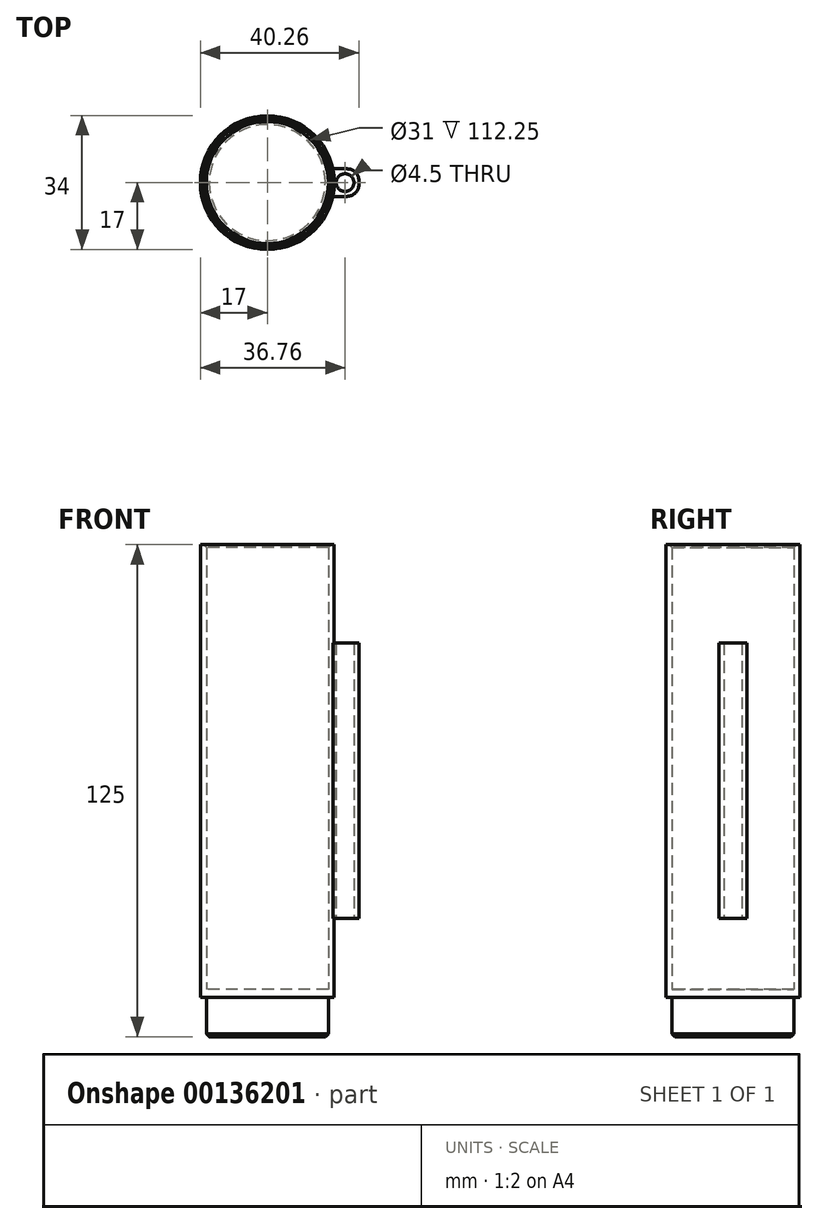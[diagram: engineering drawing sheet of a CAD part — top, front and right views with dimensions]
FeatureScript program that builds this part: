
annotation { "Feature Type Name" : "Feature", "Feature Type Description" : "" }
export const myFeature = defineFeature(function(context is Context, id is Id, definition is map)
    precondition{}
    {
        {
            var Q0;
            Q0=qCreatedBy(makeId("Top.planeOp"),FACE);
            cPlane(context, id + "F0", {"entities" : qUnion([Q0]), "cplaneType" : CPlaneType.OFFSET, "offset" : (107) * mm, "width" : 150 * mm, "height" : 150 * mm});
        }
        {
            var Q0;
            Q0=qCreatedBy(id+"F0.planeOp",FACE);
            var sketch = newSketch(context, id + "F1", { "sketchPlane" : qUnion([Q0])});
            skCircle(sketch, "E0", {"center": v(0, 0) * mm, "radius": 17 * mm});
            skCircle(sketch, "E1", {"center": v(0, 0) * mm, "radius": 15.5 * mm});
            skSolve(sketch);
        }
        {
            var Q0;
            Q0=qSketchRegion(id+"F1",true);
            extrude(context, id + "F2", {"entities" : qUnion([Q0]), "depth" : 115 * mm});
        }
        {
            var Q0;
            Q0=makeQuery(id+"F2.opExtrude","CAP_EDGE",EDGE,{"disambiguationData":[OSD([sQuery(id+"F1.wireOp",EDGE,"E1")])],"isStart":false});
            chamfer(context, id + "F3", {"entities" : qUnion([Q0]), "width" : .75 * mm, "tangentPropagation" : true});
        }
        {
            var Q0;
            Q0=qCreatedBy(id+"F0.planeOp",FACE);
            var sketch = newSketch(context, id + "F4", { "sketchPlane" : qUnion([Q0])});
            skCircle(sketch, "E2.0", {"center": v(0, 0) * mm, "radius": 17 * mm});
            skSolve(sketch);
        }
        {
            var Q0;
            Q0=makeQuery(id+"F4.imprint","IMPRINT",FACE,{"disambiguationData":[TD([[makeQuery(id+"F4.imprint","IMPRINT",EDGE,{"derivedFrom":sQuery(id+"F4.wireOp",EDGE,"E2.0")}),1.0]])]});
            extrude(context, id + "F5", {"entities" : qUnion([Q0]), "operationType" : NewBodyOperationType.ADD, "depth" : 2 * mm});
        }
        {
            var Q0;
            Q0=makeQuery(id+"F5.boolean.opBoolean","MERGE",FACE,{"derivedFrom":[makeQuery(id+"F2.opExtrude","CAP_FACE",FACE,{"disambiguationData":[OSD([sQuery(id+"F1.wireOp",EDGE,"E0"),sQuery(id+"F1.wireOp",EDGE,"E1")])],"isStart":true}),makeQuery(id+"F5.opExtrude","CAP_FACE",FACE,{"disambiguationData":[OSD([sQuery(id+"F4.wireOp",EDGE,"E2.0")])],"isStart":true})]});
            var sketch = newSketch(context, id + "F6", { "sketchPlane" : qUnion([Q0])});
            skCircle(sketch, "E3", {"center": v(0, 0) * mm, "radius": 15.5 * mm});
            skSolve(sketch);
        }
        {
            var Q0;
            Q0=qSketchRegion(id+"F6",true);
            extrude(context, id + "F7", {"entities" : qUnion([Q0]), "operationType" : NewBodyOperationType.ADD, "depth" : 10 * mm});
        }
        {
            var Q0;
            Q0=makeQuery(id+"F7.opExtrude","CAP_EDGE",EDGE,{"disambiguationData":[OSD([sQuery(id+"F6.wireOp",EDGE,"E3")])],"isStart":false});
            chamfer(context, id + "F8", {"entities" : qUnion([Q0]), "width" : .75 * mm, "tangentPropagation" : true});
        }
        {
            var Q0;
            Q0=qCreatedBy(id+"F0.planeOp",FACE);
            cPlane(context, id + "F9", {"entities" : qUnion([Q0]), "cplaneType" : CPlaneType.OFFSET, "offset" : 20 * mm, "width" : 150 * mm, "height" : 150 * mm});
        }
        {
            var Q0;
            Q0=qCreatedBy(id+"F9.planeOp",FACE);
            var sketch = newSketch(context, id + "F10", { "sketchPlane" : qUnion([Q0])});
            skLineSegment(sketch, "E4.bottom", {"start": v(16.26, 3.5) * mm, "end": v(20.26, 3.5) * mm});
            skLineSegment(sketch, "E4.top", {"start": v(16.26, -3.5) * mm, "end": v(20.26, -3.5) * mm});
            skLineSegment(sketch, "E4.left", {"start": v(16.26, 3.5) * mm, "end": v(16.26, -3.5) * mm});
            skLineSegment(sketch, "E4.right", {"start": v(23.26, 0.5) * mm, "end": v(23.26, -0.5) * mm});
            skPoint(sketch, "E5", {"position": v(16.26, 0) * mm});
            skCircle(sketch, "E6", {"center": v(19.76, 0) * mm, "radius": 2.25 * mm});
            skPoint(sketch, "E7.visualSharp", {"position": v(23.26, 3.5) * mm});
            skArc(sketch, "E7.filletArc", {"start": v(23.26, 0.5) * mm, "mid": v(22.38, 2.62) * mm, "end": v(20.26, 3.5) * mm});
            skPoint(sketch, "E8.visualSharp", {"position": v(23.26, -3.5) * mm});
            skArc(sketch, "E8.filletArc", {"start": v(20.26, -3.5) * mm, "mid": v(22.38, -2.62) * mm, "end": v(23.26, -0.5) * mm});
            skSolve(sketch);
        }
        {
            var Q0;
            Q0 = qSketchRegion(id + "F10", true);
            extrude(context, id + "F11", {"entities" : qUnion([Q0]), "depth" : 70 * mm});
        }
        {
            var Q0;
            Q0=makeQuery(id+"F2.opExtrude","SWEPT_BODY",BODY,{"disambiguationData":[OSD([sQuery(id+"F1.wireOp",EDGE,"E0"),sQuery(id+"F1.wireOp",EDGE,"E1")])]});
            var Q1;
            Q1=makeQuery(id+"F11.opExtrude","SWEPT_BODY",BODY,{"disambiguationData":[OSD([sQuery(id+"F10.wireOp",EDGE,"E4.bottom"),sQuery(id+"F10.wireOp",EDGE,"E4.top"),sQuery(id+"F10.wireOp",EDGE,"E4.left"),sQuery(id+"F10.wireOp",EDGE,"E4.right"),sQuery(id+"F10.wireOp",EDGE,"E6"),sQuery(id+"F10.wireOp",EDGE,"E7.filletArc"),sQuery(id+"F10.wireOp",EDGE,"E8.filletArc")])]});
            booleanBodies(context, id + "F12", {"operationType" : BooleanOperationType.SUBTRACTION, "tools" : qUnion([Q0]), "targets" : qUnion([Q1]), "keepTools" : true});
        }
    });
